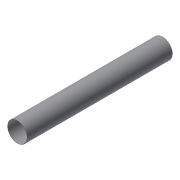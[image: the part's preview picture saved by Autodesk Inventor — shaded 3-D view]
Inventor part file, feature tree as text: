
AUTODESK INVENTOR PART (.ipt)
format: ipt  version: 2016 (Build 200138000, 138)  size: 74,240 bytes
history: native  units: in
note: dims shown in document units (in); Inventor stores cm internally (conversion verified against a paired STEP export)
features: extrude x1, sketch x1
ambient origin geometry x8: Origin, YZ Plane, XZ Plane, XY Plane, X Axis, Y Axis, Z Axis, Center Point
bodies: Solid1 (feature_tree)
feature tree (2):
  extrude  "Extrusion1"  Depth=11.811in
  sketch  "Sketch1"  dims[d1=0.0906in d2=4.3307in d3=19.685in d4=0.0in d5=11.811in d6=0.0in]
